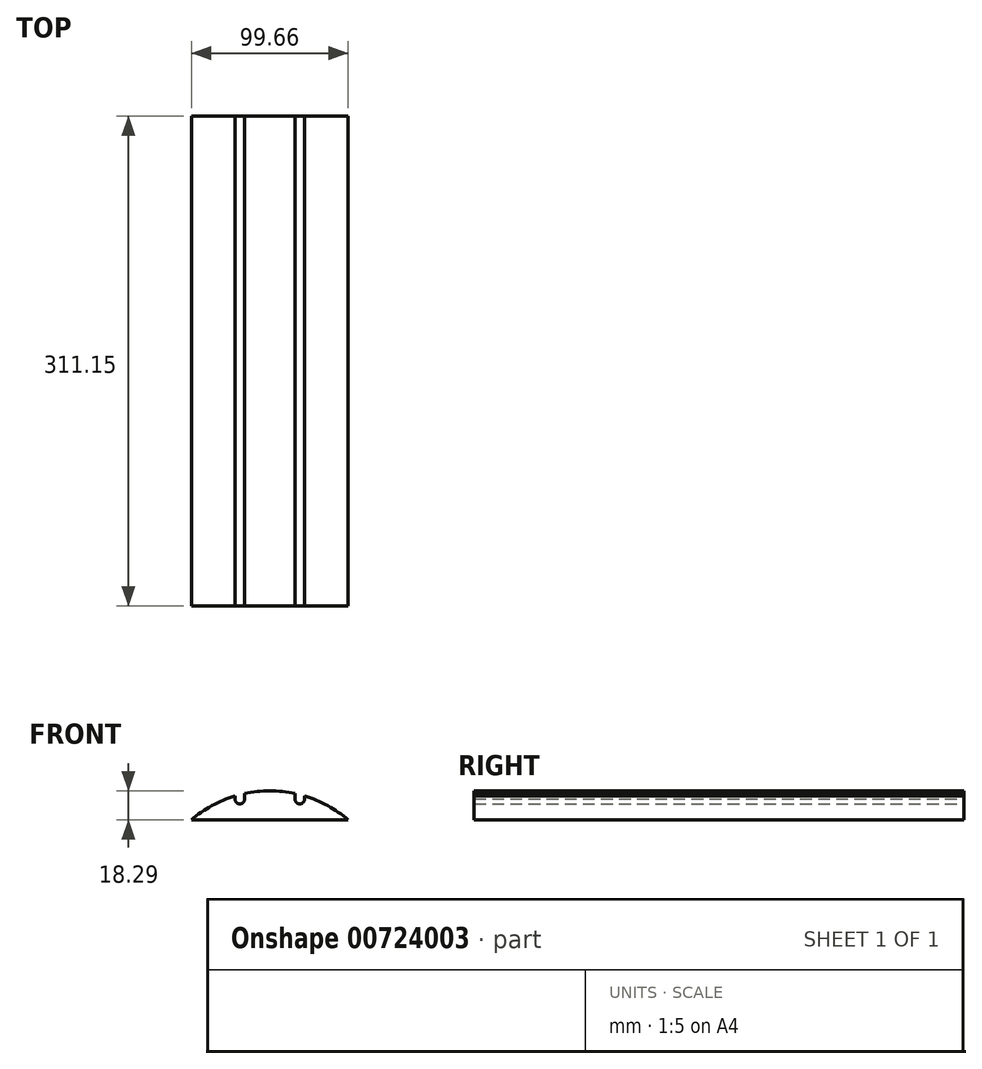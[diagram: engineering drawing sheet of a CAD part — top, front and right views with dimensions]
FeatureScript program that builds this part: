
annotation { "Feature Type Name" : "Feature", "Feature Type Description" : "" }
export const myFeature = defineFeature(function(context is Context, id is Id, definition is map)
    precondition{}
    {
        {
            var Q0;
            Q0=qCreatedBy(makeId("Front.planeOp"),FACE);
            var sketch = newSketch(context, id + "F0", { "sketchPlane" : qUnion([Q0])});
            skCircle(sketch, "E0", {"center": v(0, 0) * mm, "radius": 77.03 * mm});
            skLineSegment(sketch, "E1.bottom", {"start": v(-75.18, 58.74) * mm, "end": v(75.18, 58.74) * mm});
            skLineSegment(sketch, "E1.top", {"start": v(-75.18, -62.22) * mm, "end": v(75.18, -62.22) * mm});
            skLineSegment(sketch, "E1.left", {"start": v(-75.18, 58.74) * mm, "end": v(-75.18, -62.22) * mm});
            skLineSegment(sketch, "E1.right", {"start": v(75.18, 58.74) * mm, "end": v(75.18, -62.22) * mm});
            skCircle(sketch, "E2", {"center": v(-19.05, 71.8) * mm, "radius": 3 * mm});
            skCircle(sketch, "E3", {"center": v(19.05, 71.8) * mm, "radius": 3 * mm});
            skLineSegment(sketch, "E4.bottom", {"start": v(-22.05, 71.8) * mm, "end": v(-16.06, 71.8) * mm});
            skLineSegment(sketch, "E4.top", {"start": v(-22.05, 77.92) * mm, "end": v(-16.06, 77.92) * mm});
            skLineSegment(sketch, "E4.left", {"start": v(-22.05, 71.8) * mm, "end": v(-22.05, 77.92) * mm});
            skLineSegment(sketch, "E4.right", {"start": v(-16.06, 71.8) * mm, "end": v(-16.06, 77.92) * mm});
            skLineSegment(sketch, "E5.bottom", {"start": v(22.05, 71.8) * mm, "end": v(16.06, 71.8) * mm});
            skLineSegment(sketch, "E5.top", {"start": v(22.05, 78.56) * mm, "end": v(16.06, 78.56) * mm});
            skLineSegment(sketch, "E5.left", {"start": v(22.05, 71.8) * mm, "end": v(22.05, 78.56) * mm});
            skLineSegment(sketch, "E5.right", {"start": v(16.06, 71.8) * mm, "end": v(16.06, 78.56) * mm});
            skLineSegment(sketch, "E6.bottom", {"start": v(-50.8, 46.04) * mm, "end": v(50.8, 46.04) * mm});
            skLineSegment(sketch, "E6.top", {"start": v(-50.8, 39.69) * mm, "end": v(50.8, 39.69) * mm});
            skLineSegment(sketch, "E6.left", {"start": v(-50.8, 46.04) * mm, "end": v(-50.8, 39.69) * mm});
            skLineSegment(sketch, "E6.right", {"start": v(50.8, 46.04) * mm, "end": v(50.8, 39.69) * mm});
            skLineSegment(sketch, "E7.bottom", {"start": v(-46.05, 50.8) * mm, "end": v(-39.7, 50.8) * mm});
            skLineSegment(sketch, "E7.top", {"start": v(-46.05, -50.8) * mm, "end": v(-39.7, -50.8) * mm});
            skLineSegment(sketch, "E7.left", {"start": v(-46.05, 50.8) * mm, "end": v(-46.05, -50.8) * mm});
            skLineSegment(sketch, "E7.right", {"start": v(-39.7, 50.8) * mm, "end": v(-39.7, -50.8) * mm});
            skPoint(sketch, "E8", {"position": v(-49.83, 58.74) * mm});
            skPoint(sketch, "E9", {"position": v(49.83, 58.74) * mm});
            skSolve(sketch);
        }
        {
            var Q0;
            {var subQ1=sQuery(id+"F0.wireOp",EDGE,"E0");var subQ12=sQuery(id+"F0.wireOp",EDGE,"E5.left");var subQ15=makeQuery(id+"F0.imprint","INTERSECT",VERTEX,{"derivedFrom":[subQ1,subQ12]});Q0=makeQuery(id+"F0.imprint","IMPRINT",FACE,{"disambiguationData":[TD([[makeQuery(id+"F0.imprint","IMPRINT",EDGE,{"disambiguationData":[TD([[subQ15,1.0]])],"derivedFrom":subQ1}),1.0]])]});}
            extrude(context, id + "F1", {"entities" : qUnion([Q0]), "depth" : 311.15 * mm, "offsetDistance" : 25.4 * mm});
        }
    });
